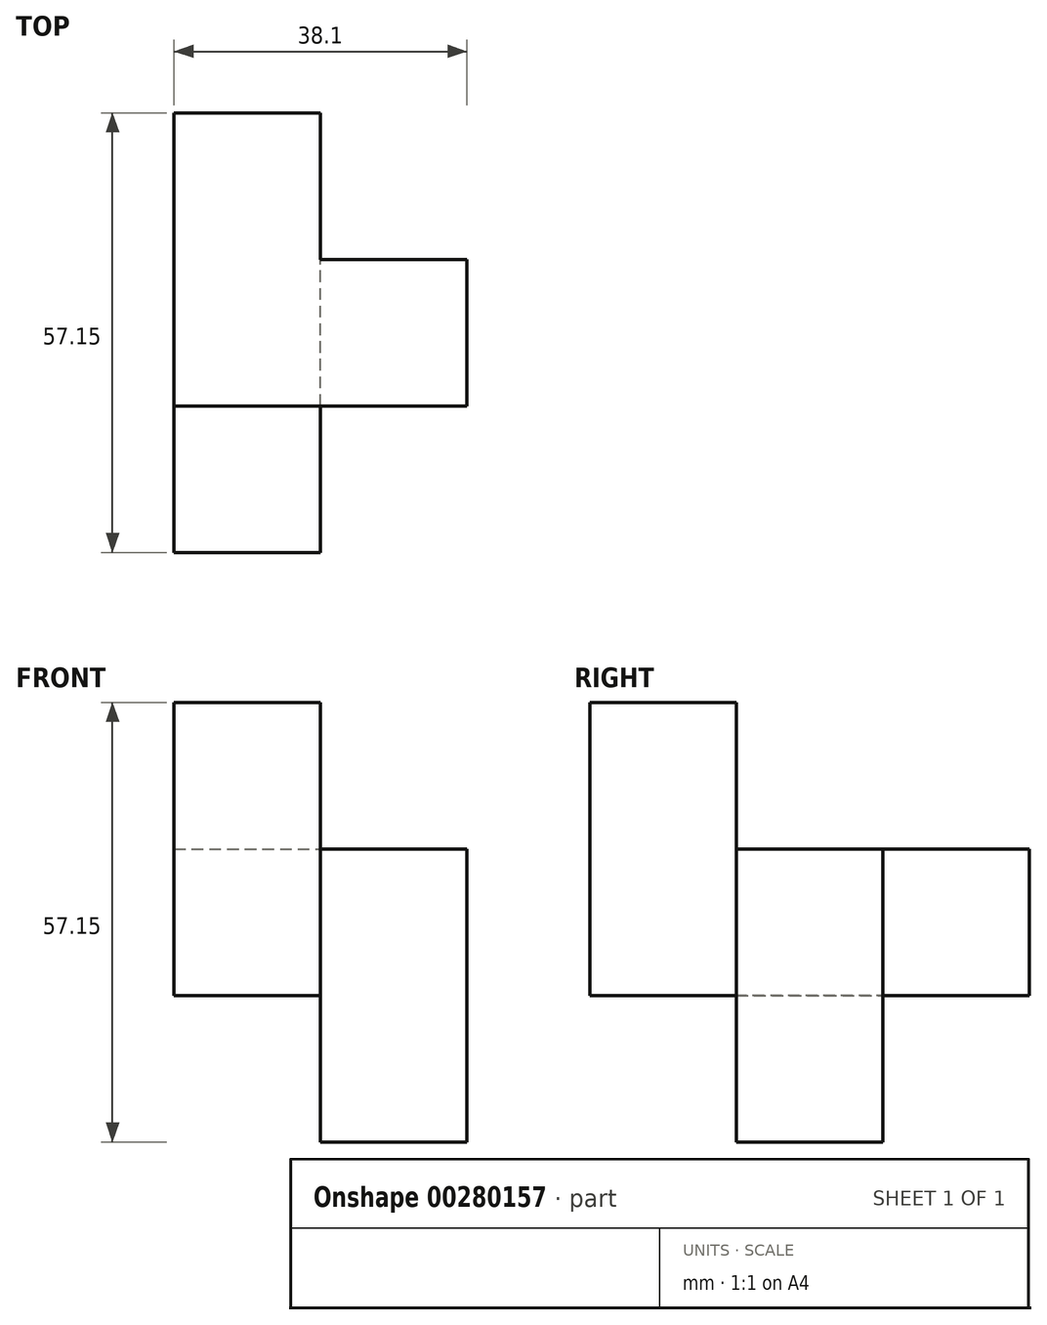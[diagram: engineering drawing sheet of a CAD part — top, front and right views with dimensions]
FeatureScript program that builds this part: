
annotation { "Feature Type Name" : "Feature", "Feature Type Description" : "" }
export const myFeature = defineFeature(function(context is Context, id is Id, definition is map)
    precondition{}
    {
        {
            var Q0;
            Q0=qCreatedBy(makeId("Top.planeOp"),FACE);
            var sketch = newSketch(context, id + "F0", { "sketchPlane" : qUnion([Q0])});
            skLineSegment(sketch, "E0.bottom", {"start": v(0, 0) * mm, "end": v(19.05, 0) * mm});
            skLineSegment(sketch, "E0.top", {"start": v(0, -57.15) * mm, "end": v(19.05, -57.15) * mm});
            skLineSegment(sketch, "E0.left", {"start": v(0, 0) * mm, "end": v(0, -57.15) * mm});
            skLineSegment(sketch, "E0.right", {"start": v(19.05, 0) * mm, "end": v(19.05, -57.15) * mm});
            skSolve(sketch);
        }
        {
            var Q0;
            Q0 = qSketchRegion(id + "F0", true);
            extrude(context, id + "F1", {"entities" : qUnion([Q0]), "depth" : 19.05 * mm});
        }
        {
            var Q0;
            Q0=makeQuery(id+"F1.opExtrude","CAP_FACE",FACE,{"disambiguationData":[OSD([sQuery(id+"F0.wireOp",EDGE,"E0.bottom"),sQuery(id+"F0.wireOp",EDGE,"E0.top"),sQuery(id+"F0.wireOp",EDGE,"E0.left"),sQuery(id+"F0.wireOp",EDGE,"E0.right")])],"isStart":false});
            var sketch = newSketch(context, id + "F2", { "sketchPlane" : qUnion([Q0])});
            skLineSegment(sketch, "E1.bottom", {"start": v(0, -57.15) * mm, "end": v(19.05, -57.15) * mm});
            skLineSegment(sketch, "E1.top", {"start": v(0, -38.1) * mm, "end": v(19.05, -38.1) * mm});
            skLineSegment(sketch, "E1.left", {"start": v(0, -57.15) * mm, "end": v(0, -38.1) * mm});
            skLineSegment(sketch, "E1.right", {"start": v(19.05, -57.15) * mm, "end": v(19.05, -38.1) * mm});
            skSolve(sketch);
        }
        {
            var Q0;
            Q0 = qSketchRegion(id + "F2", true);
            extrude(context, id + "F3", {"entities" : qUnion([Q0]), "operationType" : NewBodyOperationType.ADD, "depth" : 19.05 * mm});
        }
        {
            var Q0;
            Q0=makeQuery(id+"F3.boolean.opBoolean","MERGE",FACE,{"derivedFrom":[makeQuery(id+"F1.opExtrude","SWEPT_FACE",FACE,{"disambiguationData":[OSD([sQuery(id+"F0.wireOp",EDGE,"E0.right")])]}),makeQuery(id+"F3.opExtrude","SWEPT_FACE",FACE,{"disambiguationData":[OSD([sQuery(id+"F2.wireOp",EDGE,"E1.right")])]})]});
            var sketch = newSketch(context, id + "F4", { "sketchPlane" : qUnion([Q0])});
            skLineSegment(sketch, "E2.bottom", {"start": v(-38.1, 19.05) * mm, "end": v(-19.05, 19.05) * mm});
            skLineSegment(sketch, "E2.top", {"start": v(-38.1, 0) * mm, "end": v(-19.05, 0) * mm});
            skLineSegment(sketch, "E2.left", {"start": v(-38.1, 19.05) * mm, "end": v(-38.1, 0) * mm});
            skLineSegment(sketch, "E2.right", {"start": v(-19.05, 19.05) * mm, "end": v(-19.05, 0) * mm});
            skSolve(sketch);
        }
        {
            var Q0;
            Q0 = qSketchRegion(id + "F4", true);
            extrude(context, id + "F5", {"entities" : qUnion([Q0]), "operationType" : NewBodyOperationType.ADD, "depth" : 19.05 * mm});
        }
        {
            var Q0;
            Q0=makeQuery(id+"F5.boolean.opBoolean","MERGE",FACE,{"derivedFrom":[makeQuery(id+"F1.opExtrude","CAP_FACE",FACE,{"disambiguationData":[OSD([sQuery(id+"F0.wireOp",EDGE,"E0.bottom"),sQuery(id+"F0.wireOp",EDGE,"E0.top"),sQuery(id+"F0.wireOp",EDGE,"E0.left"),sQuery(id+"F0.wireOp",EDGE,"E0.right")])],"isStart":true}),makeQuery(id+"F5.opExtrude","SWEPT_FACE",FACE,{"disambiguationData":[OSD([sQuery(id+"F4.wireOp",EDGE,"E2.top")])]})]});
            var sketch = newSketch(context, id + "F6", { "sketchPlane" : qUnion([Q0])});
            skLineSegment(sketch, "E3.bottom", {"start": v(38.1, 38.1) * mm, "end": v(19.05, 38.1) * mm});
            skLineSegment(sketch, "E3.top", {"start": v(38.1, 19.05) * mm, "end": v(19.05, 19.05) * mm});
            skLineSegment(sketch, "E3.left", {"start": v(38.1, 38.1) * mm, "end": v(38.1, 19.05) * mm});
            skLineSegment(sketch, "E3.right", {"start": v(19.05, 38.1) * mm, "end": v(19.05, 19.05) * mm});
            skSolve(sketch);
        }
        {
            var Q0;
            Q0 = qSketchRegion(id + "F6", true);
            extrude(context, id + "F7", {"entities" : qUnion([Q0]), "operationType" : NewBodyOperationType.ADD, "depth" : 19.05 * mm});
        }
    });
